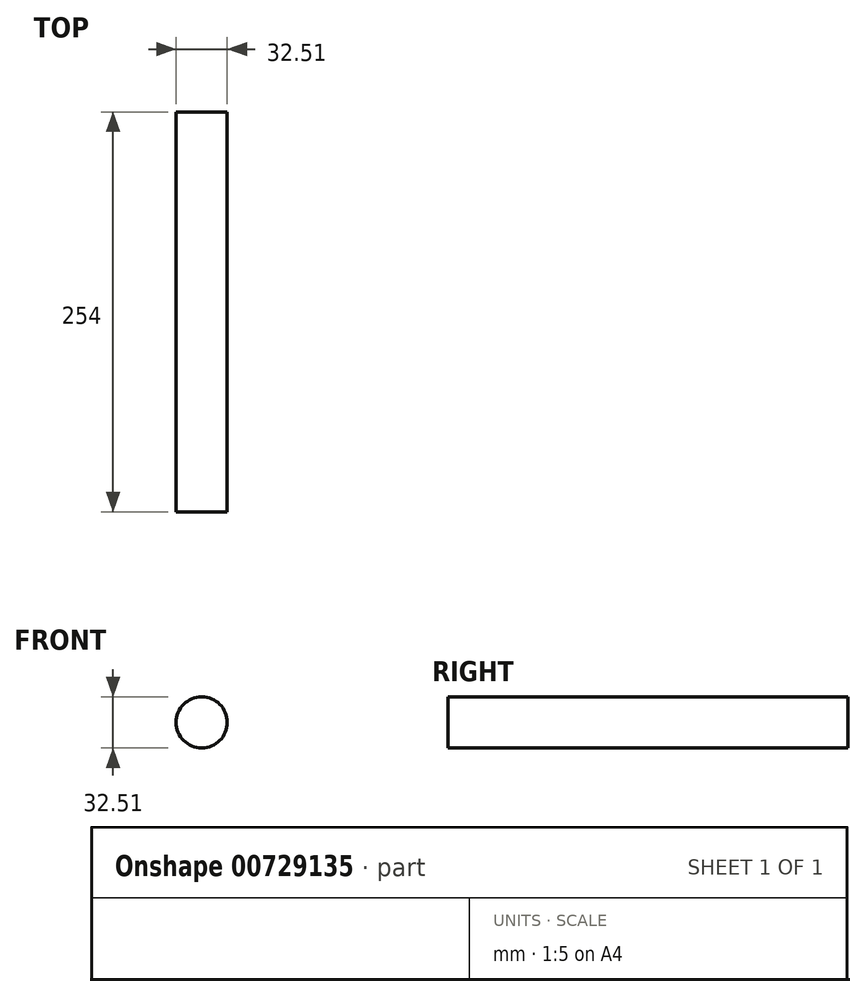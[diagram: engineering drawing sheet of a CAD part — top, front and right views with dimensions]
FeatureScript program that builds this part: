
annotation { "Feature Type Name" : "Feature", "Feature Type Description" : "" }
export const myFeature = defineFeature(function(context is Context, id is Id, definition is map)
    precondition{}
    {
        {
            var Q0;
            Q0=qCreatedBy(makeId("Front.planeOp"),FACE);
            var sketch = newSketch(context, id + "F0", { "sketchPlane" : qUnion([Q0])});
            skCircle(sketch, "E0", {"center": v(-21.12, 39.32) * mm, "radius": 16.26 * mm});
            skSolve(sketch);
        }
        {
            var Q0;
            Q0=makeQuery(id+"F0.imprint","IMPRINT",FACE,{"disambiguationData":[TD([[makeQuery(id+"F0.imprint","IMPRINT",EDGE,{"derivedFrom":sQuery(id+"F0.wireOp",EDGE,"E0")}),1.0]])]});
            extrude(context, id + "F1", {"entities" : qUnion([Q0]), "depth" : 254 * mm, "offsetDistance" : 25.4 * mm});
        }
    });
